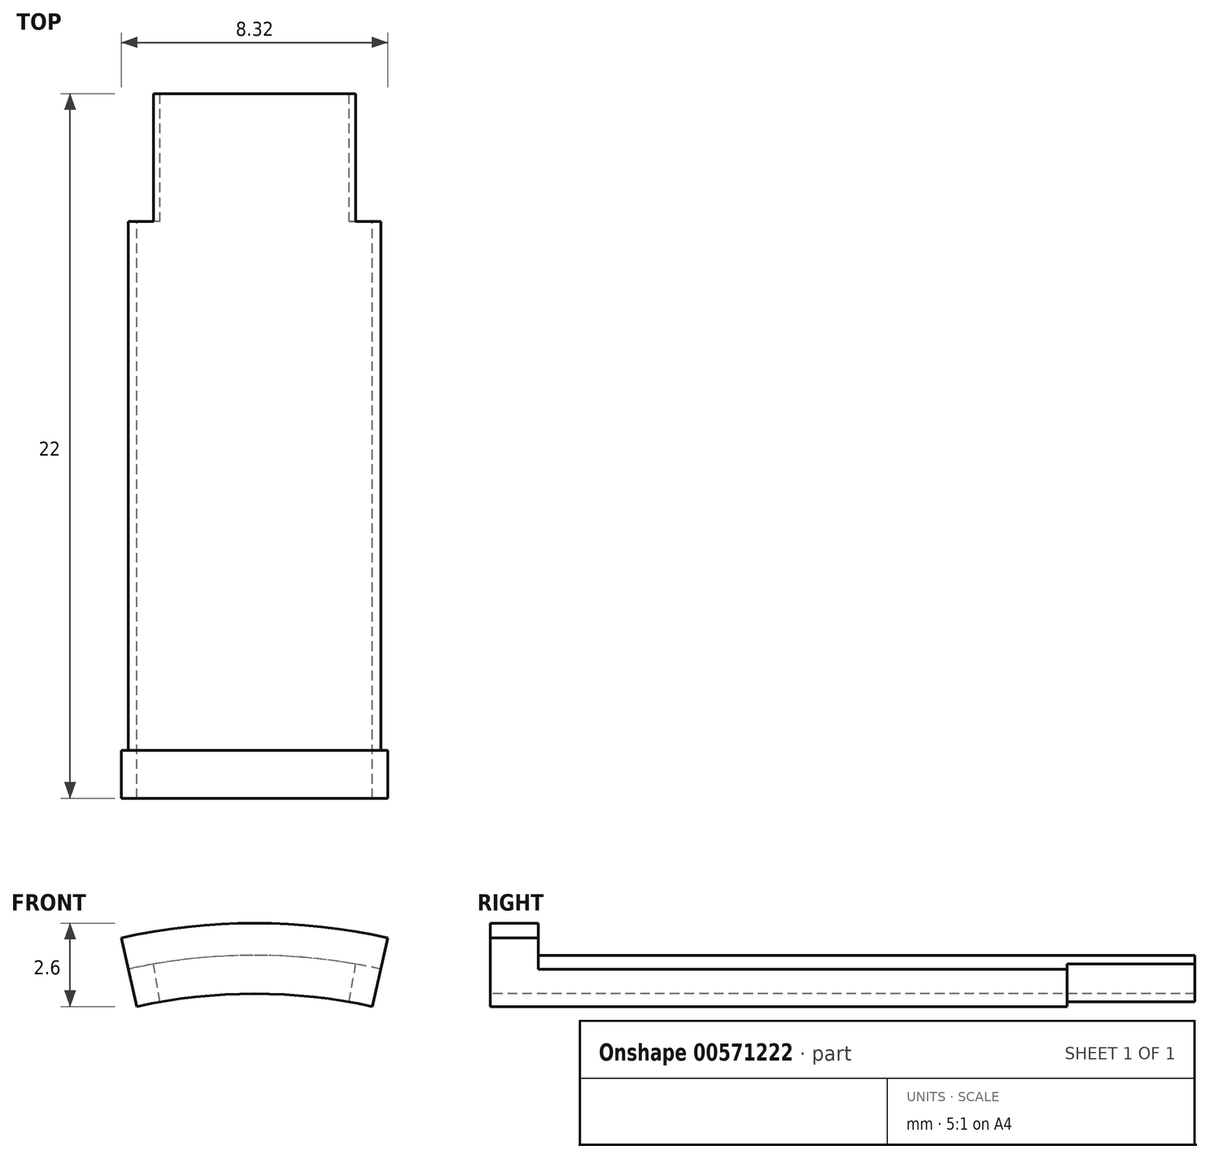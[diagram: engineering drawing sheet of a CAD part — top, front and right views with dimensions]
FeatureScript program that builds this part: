
annotation { "Feature Type Name" : "Feature", "Feature Type Description" : "" }
export const myFeature = defineFeature(function(context is Context, id is Id, definition is map)
    precondition{}
    {
        {
            var Q0;
            Q0=qCreatedBy(makeId("Right.planeOp"),FACE);
            var sketch = newSketch(context, id + "F0", { "sketchPlane" : qUnion([Q0])});
            skLineSegment(sketch, "E0", {"start": v(-16.5, 18.2) * mm, "end": v(-16.5, 19.2) * mm});
            skLineSegment(sketch, "E1", {"start": v(-16.5, 19.2) * mm, "end": v(-18, 19.2) * mm});
            skLineSegment(sketch, "E2", {"start": v(-18, 19.2) * mm, "end": v(-18, 17) * mm});
            skLineSegment(sketch, "E3", {"start": v(-18, 17) * mm, "end": v(0, 17) * mm});
            skLineSegment(sketch, "E4", {"start": v(-108.82, 0) * mm, "end": v(123.32, 0) * mm, "construction": true});
            skLineSegment(sketch, "E5", {"start": v(0, 17) * mm, "end": v(0, 18.2) * mm});
            skLineSegment(sketch, "E6", {"start": v(0, 18.2) * mm, "end": v(-16.5, 18.2) * mm});
            skSolve(sketch);
        }
        {
            var Q0;
            Q0=makeQuery(id+"F0.imprint","IMPRINT",FACE,{"disambiguationData":[TD([[makeQuery(id+"F0.imprint","IMPRINT",EDGE,{"derivedFrom":sQuery(id+"F0.wireOp",EDGE,"E0")}),1.0]])]});
            var Q1;
            Q1=sQuery(id+"F0.wireOp",EDGE,"E4");
            revolve(context, id + "F1", {"entities" : qUnion([Q0]), "axis" : qUnion([Q1]), "revolveType" : RevolveType.TWO_DIRECTIONS, "angle" : 12.5 * degree, "angleBack" : 347.5 * degree});
        }
        {
            var Q0;
            Q0=qCreatedBy(makeId("Right.planeOp"),FACE);
            var sketch = newSketch(context, id + "F2", { "sketchPlane" : qUnion([Q0])});
            skLineSegment(sketch, "E7", {"start": v(0, 17) * mm, "end": v(4, 17) * mm});
            skLineSegment(sketch, "E8", {"start": v(0, 17) * mm, "end": v(0, 18.2) * mm});
            skLineSegment(sketch, "E9", {"start": v(0, 18.2) * mm, "end": v(4, 18.2) * mm});
            skLineSegment(sketch, "E10", {"start": v(4, 18.2) * mm, "end": v(4, 17) * mm});
            skSolve(sketch);
        }
        {
            var Q0;
            Q0=qSketchRegion(id+"F2",true);
            var Q1;
            Q1=sQuery(id+"F0.wireOp",EDGE,"E4");
            revolve(context, id + "F3", {"operationType" : NewBodyOperationType.ADD, "entities" : qUnion([Q0]), "axis" : qUnion([Q1]), "revolveType" : RevolveType.TWO_DIRECTIONS, "angle" : 10 * degree, "angleBack" : 350 * degree});
        }
    });
